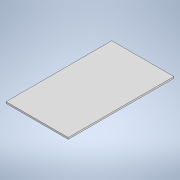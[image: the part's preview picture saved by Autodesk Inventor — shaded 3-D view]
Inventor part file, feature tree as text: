
AUTODESK INVENTOR PART (.ipt)
format: ipt  version: 2021 (Build 250183000, 183)  size: 99,328 bytes
history: native  units: in
note: dims shown in document units (in); Inventor stores cm internally (conversion verified against a paired STEP export)
features: extrude x1, sketch x1
ambient origin geometry x8: Origin, YZ Plane, XZ Plane, XY Plane, X Axis, Y Axis, Z Axis, Center Point
bodies: Solid1 (feature_tree)
feature tree (2):
  extrude  "Extrusion1"  Depth=39.3701in
  sketch  "Sketch1"  dims[d0=66.9291in d1=39.3701in d2=1.0in d3=0.0in]
